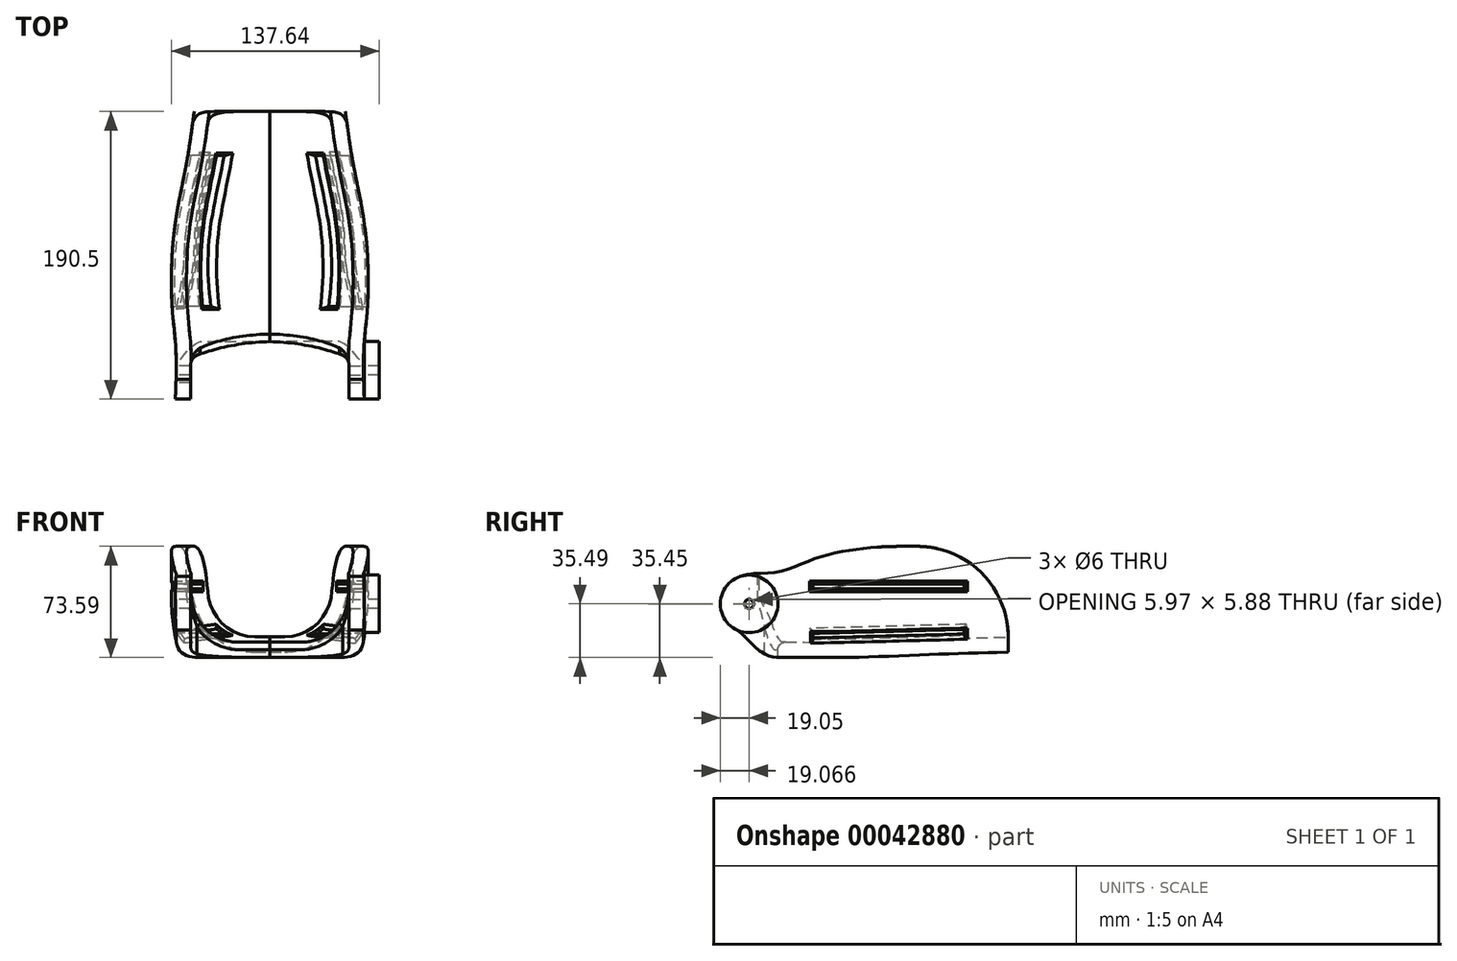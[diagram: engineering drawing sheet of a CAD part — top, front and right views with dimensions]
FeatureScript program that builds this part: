
annotation { "Feature Type Name" : "Feature", "Feature Type Description" : "" }
export const myFeature = defineFeature(function(context is Context, id is Id, definition is map)
    precondition{}
    {
        {
            assignVariable(context, id + "F0", {"name" : "FST", "anyValue" : 10 * mm});
        }
        {
            assignVariable(context, id + "F1", {"name" : "FSG", "anyValue" : 5 * mm});
        }
        {
            var Q0;
            Q0=qCreatedBy(makeId("Right.planeOp"),FACE);
            cPlane(context, id + "F2", {"entities" : qUnion([Q0]), "cplaneType" : CPlaneType.OFFSET, "offset" : (115 * mm / 2) + getVariable(context, 'FSG'), "width" : 150 * mm, "height" : 150 * mm});
        }
        {
            var Q0;
            Q0=qCreatedBy(makeId("Front.planeOp"),FACE);
            cPlane(context, id + "F3", {"entities" : qUnion([Q0]), "cplaneType" : CPlaneType.OFFSET, "offset" : 114.3 * mm, "width" : 150 * mm, "height" : 150 * mm});
        }
        {
            var Q0;
            Q0=qCreatedBy(makeId("Front.planeOp"),FACE);
            cPlane(context, id + "F4", {"entities" : qUnion([Q0]), "cplaneType" : CPlaneType.OFFSET, "offset" : 76.2 * mm, "width" : 150 * mm, "height" : 150 * mm});
        }
        {
            var Q0;
            Q0=qCreatedBy(makeId("Front.planeOp"),FACE);
            cPlane(context, id + "F5", {"entities" : qUnion([Q0]), "cplaneType" : CPlaneType.OFFSET, "offset" : (76.2 * mm) - 15 * mm, "width" : 150 * mm, "height" : 150 * mm});
        }
        {
            var Q0;
            Q0=qCreatedBy(makeId("Front.planeOp"),FACE);
            cPlane(context, id + "F6", {"entities" : qUnion([Q0]), "cplaneType" : CPlaneType.OFFSET, "offset" : (76.2 * mm) - 49 * mm, "width" : 150 * mm, "height" : 150 * mm});
        }
        {
            var Q0;
            Q0=qCreatedBy(makeId("Top.planeOp"),FACE);
            cPlane(context, id + "F7", {"entities" : qUnion([Q0]), "cplaneType" : CPlaneType.OFFSET, "offset" : 63.5 * mm + 10 * mm, "oppositeDirection" : true, "width" : 150 * mm, "height" : 150 * mm});
        }
        {
            var Q0;
            Q0=qCreatedBy(makeId("Front.planeOp"),FACE);
            cPlane(context, id + "F8", {"entities" : qUnion([Q0]), "cplaneType" : CPlaneType.OFFSET, "offset" : 76.2 * mm, "oppositeDirection" : true, "width" : 150 * mm, "height" : 150 * mm});
        }
        {
            var Q0;
            Q0=qCreatedBy(makeId("Front.planeOp"),FACE);
            cPlane(context, id + "F9", {"entities" : qUnion([Q0]), "cplaneType" : CPlaneType.OFFSET, "offset" : 76.2 * mm - 33.4 * mm, "oppositeDirection" : true, "width" : 150 * mm, "height" : 150 * mm});
        }
        {
            var Q0;
            Q0=qCreatedBy(makeId("Front.planeOp"),FACE);
            cPlane(context, id + "F10", {"entities" : qUnion([Q0]), "cplaneType" : CPlaneType.OFFSET, "offset" : 76.2 * mm - 73.4 * mm, "oppositeDirection" : true, "width" : 150 * mm, "height" : 150 * mm});
        }
        {
            var Q0;
            Q0=qCreatedBy(makeId("Top.planeOp"),FACE);
            var sketch = newSketch(context, id + "F11", { "sketchPlane" : qUnion([Q0])});
            skLineSegment(sketch, "E0", {"start": v(0, 76.2) * mm, "end": v(0, -76.2) * mm, "construction": true});
            skPoint(sketch, "E1", {"position": v(0, 0) * mm});
            skLineSegment(sketch, "E2", {"start": v(0, -76.2) * mm, "end": v(52.5, -76.2) * mm, "construction": true});
            skLineSegment(sketch, "E3", {"start": v(0, -61.2) * mm, "end": v(54, -61.2) * mm, "construction": true});
            skLineSegment(sketch, "E4", {"start": v(0, -27.2) * mm, "end": v(55, -27.2) * mm, "construction": true});
            skLineSegment(sketch, "E5", {"start": v(0, 2.8) * mm, "end": v(52.5, 2.8) * mm, "construction": true});
            skLineSegment(sketch, "E6", {"start": v(0, 42.8) * mm, "end": v(45, 42.8) * mm, "construction": true});
            skLineSegment(sketch, "E7", {"start": v(0, 76.2) * mm, "end": v(40, 76.2) * mm, "construction": true});
            skLineSegment(sketch, "E8.bottom", {"start": v(-157.02, 34.24) * mm, "end": v(-106.22, 34.24) * mm});
            skLineSegment(sketch, "E8.top", {"start": v(-157.02, -16.56) * mm, "end": v(-106.22, -16.56) * mm});
            skLineSegment(sketch, "E8.left", {"start": v(-157.02, 34.24) * mm, "end": v(-157.02, -16.56) * mm});
            skLineSegment(sketch, "E8.right", {"start": v(-106.22, 34.24) * mm, "end": v(-106.22, -16.56) * mm});
            skLineSegment(sketch, "E9", {"start": v(55, 76.2) * mm, "end": v(55, -76.2) * mm, "construction": true});
            skPoint(sketch, "E10", {"position": v(20, 76.2) * mm});
            skLineSegment(sketch, "E11", {"start": v(-60, 76.2) * mm, "end": v(-60, -76.2) * mm, "construction": true});
            skLineSegment(sketch, "E12", {"start": v(0, -95.25) * mm, "end": v(57.5, -95.25) * mm, "construction": true});
            skLineSegment(sketch, "E13", {"start": v(0, -114.3) * mm, "end": v(57.5, -114.3) * mm, "construction": true});
            skLineSegment(sketch, "E14", {"start": v(0, -84.2) * mm, "end": v(57.5, -84.2) * mm, "construction": true});
            skPoint(sketch, "E15.visualSharp", {"position": v(57.5, -84.2) * mm});
            skLineSegment(sketch, "E15.filletArc", {"start": v(57.5, -84.2) * mm, "end": v(57.5, -84.2) * mm});
            skLineSegment(sketch, "E16", {"start": v(40, 76.2) * mm, "end": v(50, 76.2) * mm});
            skLineSegment(sketch, "E17", {"start": v(45, 42.8) * mm, "end": v(55, 42.8) * mm, "construction": true});
            skLineSegment(sketch, "E18", {"start": v(52.5, 2.8) * mm, "end": v(62.5, 2.8) * mm, "construction": true});
            skLineSegment(sketch, "E19", {"start": v(55, -27.2) * mm, "end": v(65, -27.2) * mm, "construction": true});
            skLineSegment(sketch, "E20", {"start": v(54, -61.2) * mm, "end": v(64, -61.2) * mm, "construction": true});
            skLineSegment(sketch, "E21", {"start": v(52.5, -76.2) * mm, "end": v(62.5, -76.2) * mm, "construction": true});
            skLineSegment(sketch, "E22", {"start": v(57.5, -84.2) * mm, "end": v(67.5, -84.2) * mm});
            skLineSegment(sketch, "E23", {"start": v(57.5, -95.25) * mm, "end": v(67.5, -95.25) * mm});
            skLineSegment(sketch, "E24", {"start": v(57.5, -114.3) * mm, "end": v(67.5, -114.3) * mm});
            skFitSpline(sketch, "E25", {"points": [v(50, 76.2) * mm, v(55, 42.8) * mm, v(62.5, 2.8) * mm, v(65, -27.2) * mm, v(64, -61.2) * mm, v(62.5, -76.2) * mm, v(67.5, -84.2) * mm, v(67.5, -95.25) * mm, v(67.5, -114.3) * mm], "startDerivative": vector(28.82, -213.97) * mm, "endDerivative": vector(-0.1, -161.58) * mm});
            skLineSegment(sketch, "E26", {"start": v(55, -76.2) * mm, "end": v(55, -137.07) * mm, "construction": true});
            skFitSpline(sketch, "E27", {"points": [v(40, 76.2) * mm, v(45, 42.8) * mm, v(52.5, 2.8) * mm, v(55, -27.2) * mm, v(54, -61.2) * mm, v(52.5, -76.2) * mm, v(57.5, -84.2) * mm, v(57.5, -95.25) * mm, v(57.5, -114.3) * mm], "startDerivative": vector(29.26, -219.54) * mm, "endDerivative": vector(0.26, -174.77) * mm});
            skLineSegment(sketch, "E28", {"start": v(0, -114.05) * mm, "end": v(57.5, -114.05) * mm, "construction": true});
            skLineSegment(sketch, "E29", {"start": v(57.5, -114.05) * mm, "end": v(67.5, -114.05) * mm});
            skSolve(sketch);
        }
        {
            var Q0;
            Q0=qCreatedBy(id+"F3.planeOp",FACE);
            var sketch = newSketch(context, id + "F12", { "sketchPlane" : qUnion([Q0])});
            skLineSegment(sketch, "E30", {"start": v(0, 0) * mm, "end": v(52.5, 0) * mm, "construction": true});
            skLineSegment(sketch, "E31", {"start": v(52.5, 0) * mm, "end": v(62.5, 0) * mm});
            skLineSegment(sketch, "E32", {"start": v(0, 0) * mm, "end": v(0, -63.5) * mm, "construction": true});
            skLineSegment(sketch, "E33", {"start": v(0, 0) * mm, "end": v(47.5, 0) * mm, "construction": true});
            skLineSegment(sketch, "E34", {"start": v(52.5, 0) * mm, "end": v(52.5, -31.5) * mm});
            skLineSegment(sketch, "E35", {"start": v(20.5, -63.5) * mm, "end": v(0, -63.5) * mm});
            skLineSegment(sketch, "E36", {"start": v(0, -63.5) * mm, "end": v(0, -73.5) * mm});
            skArc(sketch, "E37.filletArc", {"start": v(20.5, -63.5) * mm, "mid": v(43.13, -54.13) * mm, "end": v(52.5, -31.5) * mm});
            skPoint(sketch, "E38", {"position": v(0, -35.5) * mm});
            skLineSegment(sketch, "E39", {"start": v(0, -35.5) * mm, "end": v(67.5, -35.5) * mm, "construction": true});
            skLineSegment(sketch, "E40", {"start": v(62.5, 0) * mm, "end": v(62.5, -58.5) * mm});
            skLineSegment(sketch, "E41", {"start": v(47.5, -73.5) * mm, "end": v(0, -73.5) * mm});
            skPoint(sketch, "E42.visualSharp", {"position": v(62.5, -73.5) * mm});
            skArc(sketch, "E42.filletArc", {"start": v(47.5, -73.5) * mm, "mid": v(58.1, -69.1) * mm, "end": v(62.5, -58.5) * mm});
            skSolve(sketch);
        }
        {
            var Q0;
            Q0=qCreatedBy(id+"F4.planeOp",FACE);
            var sketch = newSketch(context, id + "F13", { "sketchPlane" : qUnion([Q0])});
            skLineSegment(sketch, "E43", {"start": v(0, 0) * mm, "end": v(52.5, 0) * mm, "construction": true});
            skLineSegment(sketch, "E44", {"start": v(0, 0) * mm, "end": v(0, -63.5) * mm, "construction": true});
            skLineSegment(sketch, "E45", {"start": v(52.5, 0) * mm, "end": v(62.5, 0) * mm});
            skLineSegment(sketch, "E46", {"start": v(0, -63.5) * mm, "end": v(0, -73.5) * mm});
            skLineSegment(sketch, "E47", {"start": v(52.5, 0) * mm, "end": v(52.5, -31.5) * mm});
            skLineSegment(sketch, "E48", {"start": v(20.5, -63.5) * mm, "end": v(0, -63.5) * mm});
            skLineSegment(sketch, "E49", {"start": v(62.5, -58.5) * mm, "end": v(62.5, 0) * mm});
            skPoint(sketch, "E50.visualSharp", {"position": v(52.5, -63.5) * mm});
            skArc(sketch, "E50.filletArc", {"start": v(20.5, -63.5) * mm, "mid": v(43.13, -54.13) * mm, "end": v(52.5, -31.5) * mm});
            skLineSegment(sketch, "E51", {"start": v(47.5, -73.5) * mm, "end": v(0, -73.5) * mm});
            skPoint(sketch, "E52.visualSharp", {"position": v(62.5, -73.5) * mm});
            skArc(sketch, "E52.filletArc", {"start": v(47.5, -73.5) * mm, "mid": v(58.1, -69.1) * mm, "end": v(62.5, -58.5) * mm});
            skSolve(sketch);
        }
        {
            var Q0;
            Q0=qCreatedBy(id+"F5.planeOp",FACE);
            var sketch = newSketch(context, id + "F14", { "sketchPlane" : qUnion([Q0])});
            skLineSegment(sketch, "E53", {"start": v(0, 0) * mm, "end": v(54, 0) * mm, "construction": true});
            skLineSegment(sketch, "E54", {"start": v(0, 0) * mm, "end": v(0, -63.5) * mm, "construction": true});
            skLineSegment(sketch, "E55", {"start": v(54, 0) * mm, "end": v(64, 0) * mm});
            skLineSegment(sketch, "E56", {"start": v(0, -63.5) * mm, "end": v(0, -73.5) * mm});
            skLineSegment(sketch, "E57", {"start": v(54, 0) * mm, "end": v(54, -31.5) * mm});
            skLineSegment(sketch, "E58", {"start": v(22, -63.5) * mm, "end": v(0, -63.5) * mm});
            skLineSegment(sketch, "E59", {"start": v(64, 0) * mm, "end": v(64, -48.5) * mm});
            skLineSegment(sketch, "E60", {"start": v(39, -73.5) * mm, "end": v(0, -73.5) * mm});
            skPoint(sketch, "E61.visualSharp", {"position": v(54, -63.5) * mm});
            skArc(sketch, "E61.filletArc", {"start": v(22, -63.5) * mm, "mid": v(44.63, -54.13) * mm, "end": v(54, -31.5) * mm});
            skPoint(sketch, "E62.visualSharp", {"position": v(64, -73.5) * mm});
            skArc(sketch, "E62.filletArc", {"start": v(39, -73.5) * mm, "mid": v(56.68, -66.18) * mm, "end": v(64, -48.5) * mm});
            skSolve(sketch);
        }
        {
            var Q0;
            Q0=qCreatedBy(id+"F6.planeOp",FACE);
            var sketch = newSketch(context, id + "F15", { "sketchPlane" : qUnion([Q0])});
            skLineSegment(sketch, "E63", {"start": v(0, 0) * mm, "end": v(55, 0) * mm, "construction": true});
            skLineSegment(sketch, "E64", {"start": v(0, 0) * mm, "end": v(0, -63.5) * mm, "construction": true});
            skLineSegment(sketch, "E65", {"start": v(55, 0) * mm, "end": v(65, 0) * mm});
            skLineSegment(sketch, "E66", {"start": v(0, -63.5) * mm, "end": v(0, -73.5) * mm});
            skLineSegment(sketch, "E67", {"start": v(55, 0) * mm, "end": v(55, -31.5) * mm});
            skLineSegment(sketch, "E68", {"start": v(23, -63.5) * mm, "end": v(0, -63.5) * mm});
            skLineSegment(sketch, "E69", {"start": v(65, 0) * mm, "end": v(65, -31.5) * mm});
            skLineSegment(sketch, "E70", {"start": v(23, -73.5) * mm, "end": v(0, -73.5) * mm});
            skPoint(sketch, "E71.visualSharp", {"position": v(55, -63.5) * mm});
            skArc(sketch, "E71.filletArc", {"start": v(23, -63.5) * mm, "mid": v(45.63, -54.13) * mm, "end": v(55, -31.5) * mm});
            skPoint(sketch, "E72.visualSharp", {"position": v(65, -73.5) * mm});
            skArc(sketch, "E72.filletArc", {"start": v(23, -73.5) * mm, "mid": v(52.7, -61.2) * mm, "end": v(65, -31.5) * mm});
            skSolve(sketch);
        }
        {
            var Q0;
            Q0=qCreatedBy(id+"F8.planeOp",FACE);
            var sketch = newSketch(context, id + "F16", { "sketchPlane" : qUnion([Q0])});
            skLineSegment(sketch, "E73", {"start": v(0, 0) * mm, "end": v(0, -60) * mm, "construction": true});
            skLineSegment(sketch, "E74", {"start": v(0, 0) * mm, "end": v(40, 0) * mm, "construction": true});
            skLineSegment(sketch, "E75", {"start": v(0, -60) * mm, "end": v(10, -60) * mm});
            skLineSegment(sketch, "E76", {"start": v(40, 0) * mm, "end": v(50, 0) * mm});
            skLineSegment(sketch, "E77", {"start": v(0, -60) * mm, "end": v(0, -70) * mm});
            skLineSegment(sketch, "E78", {"start": v(0, -70) * mm, "end": v(10, -70) * mm});
            skLineSegment(sketch, "E79", {"start": v(50, -30) * mm, "end": v(50, 0) * mm});
            skLineSegment(sketch, "E80", {"start": v(40, -30) * mm, "end": v(40, 0) * mm});
            skPoint(sketch, "E81.visualSharp", {"position": v(40, -60) * mm});
            skArc(sketch, "E81.filletArc", {"start": v(10, -60) * mm, "mid": v(31.21, -51.21) * mm, "end": v(40, -30) * mm});
            skPoint(sketch, "E82.visualSharp", {"position": v(50, -70) * mm});
            skArc(sketch, "E82.filletArc", {"start": v(10, -70) * mm, "mid": v(38.28, -58.28) * mm, "end": v(50, -30) * mm});
            skSolve(sketch);
        }
        {
            var Q0;
            Q0=qCreatedBy(id+"F9.planeOp",FACE);
            var sketch = newSketch(context, id + "F17", { "sketchPlane" : qUnion([Q0])});
            skLineSegment(sketch, "E83", {"start": v(0, 0) * mm, "end": v(45, 0) * mm, "construction": true});
            skLineSegment(sketch, "E84", {"start": v(0, 0) * mm, "end": v(0, -61) * mm, "construction": true});
            skLineSegment(sketch, "E85", {"start": v(45, 0) * mm, "end": v(55, 0) * mm});
            skLineSegment(sketch, "E86", {"start": v(0, -61) * mm, "end": v(0, -71) * mm});
            skLineSegment(sketch, "E87", {"start": v(45, 0) * mm, "end": v(45, -31) * mm});
            skLineSegment(sketch, "E88", {"start": v(15, -61) * mm, "end": v(0, -61) * mm});
            skLineSegment(sketch, "E89", {"start": v(55, 0) * mm, "end": v(55, -31) * mm});
            skLineSegment(sketch, "E90", {"start": v(15, -71) * mm, "end": v(0, -71) * mm});
            skPoint(sketch, "E91.visualSharp", {"position": v(45, -61) * mm});
            skArc(sketch, "E91.filletArc", {"start": v(15, -61) * mm, "mid": v(36.21, -52.21) * mm, "end": v(45, -31) * mm});
            skPoint(sketch, "E92.visualSharp", {"position": v(55, -71) * mm});
            skArc(sketch, "E92.filletArc", {"start": v(15, -71) * mm, "mid": v(43.28, -59.28) * mm, "end": v(55, -31) * mm});
            skSolve(sketch);
        }
        {
            var Q0;
            Q0=qCreatedBy(id+"F10.planeOp",FACE);
            var sketch = newSketch(context, id + "F18", { "sketchPlane" : qUnion([Q0])});
            skLineSegment(sketch, "E93", {"start": v(0, 0) * mm, "end": v(52.5, 0) * mm, "construction": true});
            skLineSegment(sketch, "E94", {"start": v(0, 0) * mm, "end": v(0, -62.5) * mm, "construction": true});
            skLineSegment(sketch, "E95", {"start": v(52.5, 0) * mm, "end": v(62.5, 0) * mm});
            skLineSegment(sketch, "E96", {"start": v(0, -62.5) * mm, "end": v(0, -72.5) * mm});
            skLineSegment(sketch, "E97", {"start": v(52.5, 0) * mm, "end": v(52.5, -31.5) * mm});
            skLineSegment(sketch, "E98", {"start": v(21.5, -62.5) * mm, "end": v(0, -62.5) * mm});
            skLineSegment(sketch, "E99", {"start": v(62.5, 0) * mm, "end": v(62.5, -31.5) * mm});
            skLineSegment(sketch, "E100", {"start": v(21.5, -72.5) * mm, "end": v(0, -72.5) * mm});
            skPoint(sketch, "E101.visualSharp", {"position": v(52.5, -62.5) * mm});
            skArc(sketch, "E101.filletArc", {"start": v(21.5, -62.5) * mm, "mid": v(43.42, -53.42) * mm, "end": v(52.5, -31.5) * mm});
            skPoint(sketch, "E102.visualSharp", {"position": v(62.5, -72.5) * mm});
            skArc(sketch, "E102.filletArc", {"start": v(21.5, -72.5) * mm, "mid": v(50.5, -60.5) * mm, "end": v(62.5, -31.5) * mm});
            skSolve(sketch);
        }
        {
            var Q0;
            Q0=qCreatedBy(makeId("Right.planeOp"),FACE);
            var sketch = newSketch(context, id + "F19", { "sketchPlane" : qUnion([Q0])});
            skLineSegment(sketch, "E103", {"start": v(-76.2, 0) * mm, "end": v(76.2, 0) * mm, "construction": true});
            skLineSegment(sketch, "E104", {"start": v(76.2, 0) * mm, "end": v(76.2, -60) * mm, "construction": true});
            skLineSegment(sketch, "E105", {"start": v(42.8, 0) * mm, "end": v(42.8, -61) * mm, "construction": true});
            skLineSegment(sketch, "E106", {"start": v(2.8, 0) * mm, "end": v(2.8, -62.5) * mm, "construction": true});
            skLineSegment(sketch, "E107", {"start": v(-27.2, 0) * mm, "end": v(-27.2, -63.5) * mm, "construction": true});
            skLineSegment(sketch, "E108", {"start": v(-61.2, 0) * mm, "end": v(-61.2, -63.5) * mm, "construction": true});
            skLineSegment(sketch, "E109", {"start": v(-76.2, 0) * mm, "end": v(-76.2, -63.5) * mm, "construction": true});
            skPoint(sketch, "E110", {"position": v(0, 0) * mm});
            skLineSegment(sketch, "E111", {"start": v(76.2, -60) * mm, "end": v(76.2, -70) * mm});
            skLineSegment(sketch, "E112", {"start": v(42.8, -61) * mm, "end": v(42.8, -71) * mm});
            skLineSegment(sketch, "E113", {"start": v(2.8, -62.5) * mm, "end": v(2.8, -72.5) * mm});
            skLineSegment(sketch, "E114", {"start": v(-27.2, -63.5) * mm, "end": v(-27.2, -73.5) * mm});
            skLineSegment(sketch, "E115", {"start": v(-61.2, -63.5) * mm, "end": v(-61.2, -73.5) * mm});
            skLineSegment(sketch, "E116", {"start": v(-76.2, -63.5) * mm, "end": v(-76.2, -73.5) * mm});
            skLineSegment(sketch, "E117", {"start": v(-84.2, 0) * mm, "end": v(-84.2, -63.5) * mm, "construction": true});
            skLineSegment(sketch, "E118", {"start": v(-84.2, -63.5) * mm, "end": v(-84.2, -73.5) * mm});
            skLineSegment(sketch, "E119", {"start": v(-95.25, 0) * mm, "end": v(-95.25, -63.5) * mm, "construction": true});
            skLineSegment(sketch, "E120", {"start": v(-114.3, 0) * mm, "end": v(-114.3, -63.5) * mm, "construction": true});
            skLineSegment(sketch, "E121", {"start": v(-95.25, -63.5) * mm, "end": v(-95.25, -73.5) * mm});
            skLineSegment(sketch, "E122", {"start": v(-114.3, -63.5) * mm, "end": v(-114.3, -73.5) * mm});
            skFitSpline(sketch, "E123", {"points": [v(76.2, -60) * mm, v(42.8, -61) * mm, v(2.8, -62.5) * mm, v(-27.2, -63.5) * mm, v(-61.2, -63.5) * mm, v(-76.2, -63.5) * mm, v(-84.2, -63.5) * mm, v(-95.25, -63.5) * mm, v(-114.3, -63.5) * mm], "startDerivative": vector(-217.44, -6.1) * mm, "endDerivative": vector(-173.87, 0) * mm});
            skFitSpline(sketch, "E124", {"points": [v(76.2, -70) * mm, v(42.8, -71) * mm, v(2.8, -72.5) * mm, v(-27.2, -73.5) * mm, v(-61.2, -73.5) * mm, v(-76.2, -73.5) * mm, v(-84.2, -73.5) * mm, v(-95.25, -73.5) * mm, v(-114.3, -73.5) * mm], "startDerivative": vector(-217.36, -6.1) * mm, "endDerivative": vector(-173.09, 0) * mm});
            skLineSegment(sketch, "E125.bottom", {"start": v(-173.81, 0) * mm, "end": v(-223.81, 0) * mm, "construction": true});
            skLineSegment(sketch, "E125.top", {"start": v(-173.81, -50) * mm, "end": v(-223.81, -50) * mm, "construction": true});
            skLineSegment(sketch, "E125.left", {"start": v(-173.81, 0) * mm, "end": v(-173.81, -50) * mm, "construction": true});
            skLineSegment(sketch, "E125.right", {"start": v(-223.81, 0) * mm, "end": v(-223.81, -50) * mm, "construction": true});
            skSolve(sketch);
        }
        {
            var Q0;
            Q0=makeQuery(id+"F16.imprint","IMPRINT",FACE,{"disambiguationData":[TD([[makeQuery(id+"F16.imprint","IMPRINT",EDGE,{"derivedFrom":sQuery(id+"F16.wireOp",EDGE,"E75")}),-1.0]])]});
            var Q1;
            Q1=makeQuery(id+"F17.imprint","IMPRINT",FACE,{"disambiguationData":[TD([[makeQuery(id+"F17.imprint","IMPRINT",EDGE,{"derivedFrom":sQuery(id+"F17.wireOp",EDGE,"E85")}),-1.0]])]});
            var Q2;
            Q2=makeQuery(id+"F18.imprint","IMPRINT",FACE,{"disambiguationData":[TD([[makeQuery(id+"F18.imprint","IMPRINT",EDGE,{"derivedFrom":sQuery(id+"F18.wireOp",EDGE,"E95")}),-1.0]])]});
            var Q3;
            Q3=makeQuery(id+"F15.imprint","IMPRINT",FACE,{"disambiguationData":[TD([[makeQuery(id+"F15.imprint","IMPRINT",EDGE,{"derivedFrom":sQuery(id+"F15.wireOp",EDGE,"E65")}),-1.0]])]});
            var Q4;
            Q4=makeQuery(id+"F14.imprint","IMPRINT",FACE,{"disambiguationData":[TD([[makeQuery(id+"F14.imprint","IMPRINT",EDGE,{"derivedFrom":sQuery(id+"F14.wireOp",EDGE,"E55")}),-1.0]])]});
            var Q5;
            Q5=makeQuery(id+"F13.imprint","IMPRINT",FACE,{"disambiguationData":[TD([[makeQuery(id+"F13.imprint","IMPRINT",EDGE,{"derivedFrom":sQuery(id+"F13.wireOp",EDGE,"E45")}),-1.0]])]});
            var Q6;
            Q6=makeQuery(id+"F12.imprint","IMPRINT",FACE,{"disambiguationData":[TD([[makeQuery(id+"F12.imprint","IMPRINT",EDGE,{"derivedFrom":sQuery(id+"F12.wireOp",EDGE,"E31")}),-1.0]])]});
            loft(context, id + "F20", {"sheetProfilesArray" : [{ "sheetProfileEntities" : qUnion([Q0]) }, { "sheetProfileEntities" : qUnion([Q1]) }, { "sheetProfileEntities" : qUnion([Q2]) }, { "sheetProfileEntities" : qUnion([Q3]) }, { "sheetProfileEntities" : qUnion([Q4]) }, { "sheetProfileEntities" : qUnion([Q5]) }, { "sheetProfileEntities" : qUnion([Q6]) }]});
        }
        {
            var Q0;
            Q0=makeQuery(id+"F20.opLoft","MID_CAP_EDGE",EDGE,{"disambiguationData":[OSD([sQuery(id+"F16.wireOp",EDGE,"E76"),sQuery(id+"F16.wireOp",EDGE,"E79"),sQuery(id+"F16.wireOp",EDGE,"E80")])],"capPos":0.0});
            fillet(context, id + "F21", {"entities" : qUnion([Q0]), "radius" : 60 * mm, "tangentPropagation" : true, "allowEdgeOverflow" : false});
        }
        {
            var Q0;
            Q0=qCreatedBy(id+"F2.planeOp",FACE);
            var sketch = newSketch(context, id + "F22", { "sketchPlane" : qUnion([Q0])});
            skCircle(sketch, "E126", {"center": v(-95.25, -38.1) * mm, "radius": 19.05 * mm});
            skLineSegment(sketch, "E127", {"start": v(-76.2, 0) * mm, "end": v(76.2, 0) * mm, "construction": true});
            skLineSegment(sketch, "E128", {"start": v(-76.2, 0) * mm, "end": v(-76.2, -63.5) * mm, "construction": true});
            skLineSegment(sketch, "E129", {"start": v(-76.2, -63.5) * mm, "end": v(-76.2, -73.5) * mm, "construction": true});
            skLineSegment(sketch, "E130", {"start": v(-76.2, -73.5) * mm, "end": v(-114.3, -73.5) * mm, "construction": true});
            skLineSegment(sketch, "E131", {"start": v(-76.2, -19.05) * mm, "end": v(-114.3, -19.05) * mm, "construction": true});
            skLineSegment(sketch, "E132", {"start": v(-76.2, 0) * mm, "end": v(-114.3, 0) * mm, "construction": true});
            skLineSegment(sketch, "E133", {"start": v(-95.25, -38.1) * mm, "end": v(-114.3, -38.1) * mm, "construction": true});
            skLineSegment(sketch, "E134", {"start": v(-95.25, -38.1) * mm, "end": v(-95.25, -73.5) * mm, "construction": true});
            skLineSegment(sketch, "E135", {"start": v(-127.04, -54.43) * mm, "end": v(-127.04, -88.5) * mm});
            skLineSegment(sketch, "E136", {"start": v(-127.04, -54.43) * mm, "end": v(-127.04, 0) * mm});
            skLineSegment(sketch, "E137", {"start": v(-127.04, 0) * mm, "end": v(0, 0) * mm, "construction": true});
            skLineSegment(sketch, "E138", {"start": v(-51.2, 0) * mm, "end": v(-51.2, -8) * mm, "construction": true});
            skPoint(sketch, "E139", {"position": v(-76.2, -17) * mm});
            skLineSegment(sketch, "E140", {"start": v(-16.2, 0) * mm, "end": v(-16.2, -1) * mm, "construction": true});
            skLineSegment(sketch, "E141", {"start": v(3.8, 0) * mm, "end": v(3.8, 0) * mm});
            skPoint(sketch, "E142", {"position": v(13.8, 0) * mm});
            skLineSegment(sketch, "E143", {"start": v(-127.04, 0) * mm, "end": v(-127.04, 22.7) * mm});
            skLineSegment(sketch, "E144", {"start": v(-127.04, 22.7) * mm, "end": v(13.8, 22.7) * mm});
            skLineSegment(sketch, "E145", {"start": v(13.8, 22.7) * mm, "end": v(13.8, 0) * mm});
            skCircle(sketch, "E146", {"center": v(-95.25, -38.1) * mm, "radius": 3 * mm});
            skLineSegment(sketch, "E147", {"start": v(-95.25, -38.1) * mm, "end": v(-101.14, -19.98) * mm, "construction": true});
            skLineSegment(sketch, "E148", {"start": v(-95.25, -38.1) * mm, "end": v(-95.25, -19.05) * mm, "construction": true});
            skFitSpline(sketch, "E149", {"points": [v(-101.14, -19.98) * mm, v(-76.2, -17) * mm, v(-51.2, -8) * mm, v(-16.2, -1) * mm, v(3.8, 0) * mm, v(13.8, 0) * mm], "startDerivative": vector(117.64, 43.18) * mm, "endDerivative": vector(70.79, -0.21) * mm});
            skLineSegment(sketch, "E150", {"start": v(-95.25, -38.1) * mm, "end": v(-103.3, -55.37) * mm, "construction": true});
            skLineSegment(sketch, "E151", {"start": v(-127.04, -88.5) * mm, "end": v(-76.2, -88.5) * mm});
            skLineSegment(sketch, "E152", {"start": v(-76.2, -73.5) * mm, "end": v(-76.2, -88.5) * mm});
            skFitSpline(sketch, "E153", {"points": [v(-103.3, -55.37) * mm, v(-76.2, -73.5) * mm], "startDerivative": vector(27.1, -18.13) * mm, "endDerivative": vector(39, 0) * mm});
            skSolve(sketch);
        }
        {
            var Q0;
            Q0=makeQuery(id+"F22.imprint","IMPRINT",FACE,{"disambiguationData":[TD([[makeQuery(id+"F22.imprint","IMPRINT",EDGE,{"derivedFrom":sQuery(id+"F22.wireOp",EDGE,"E135")}),1.0]])]});
            extrude(context, id + "F23", {"entities" : qUnion([Q0]), "operationType" : NewBodyOperationType.REMOVE, "endBound" : BoundingType.SYMMETRIC, "oppositeDirection" : true, "depth" : 140 * mm});
        }
        {
            var Q0;
            Q0=makeQuery(id+"F22.imprint","IMPRINT",FACE,{"disambiguationData":[TD([[makeQuery(id+"F22.imprint","IMPRINT",EDGE,{"derivedFrom":sQuery(id+"F22.wireOp",EDGE,"E146")}),1.0]])]});
            extrude(context, id + "F24", {"entities" : qUnion([Q0]), "operationType" : NewBodyOperationType.REMOVE, "endBound" : BoundingType.THROUGH_ALL, "oppositeDirection" : true, "depth" : 25 * mm});
        }
        {
            var Q0;
            Q0=qCreatedBy(id+"F7.planeOp",FACE);
            var sketch = newSketch(context, id + "F25", { "sketchPlane" : qUnion([Q0])});
            skLineSegment(sketch, "E154", {"start": v(0, 76.2) * mm, "end": v(0, -76.2) * mm});
            skLineSegment(sketch, "E155", {"start": v(0, -114.3) * mm, "end": v(52.5, -114.3) * mm});
            skLineSegment(sketch, "E156", {"start": v(0, -76.2) * mm, "end": v(0, -114.3) * mm, "construction": true});
            skLineSegment(sketch, "E157", {"start": v(0, -95.25) * mm, "end": v(52.5, -95.25) * mm, "construction": true});
            skLineSegment(sketch, "E158.rect.bottom", {"start": v(62.5, -98.25) * mm, "end": v(52.5, -98.25) * mm, "construction": true});
            skLineSegment(sketch, "E158.rect.top", {"start": v(62.5, -92.25) * mm, "end": v(52.5, -92.25) * mm, "construction": true});
            skLineSegment(sketch, "E158.rect.left", {"start": v(62.5, -98.25) * mm, "end": v(62.5, -92.25) * mm, "construction": true});
            skLineSegment(sketch, "E158.rect.right", {"start": v(52.5, -98.25) * mm, "end": v(52.5, -92.25) * mm, "construction": true});
            skPoint(sketch, "E158.rect.middle", {"position": v(57.5, -95.25) * mm});
            skLineSegment(sketch, "E159", {"start": v(52.5, -95.25) * mm, "end": v(52.5, -92.25) * mm, "construction": true});
            skLineSegment(sketch, "E160", {"start": v(0, -72.2) * mm, "end": v(-24.84, -72.2) * mm, "construction": true});
            skLineSegment(sketch, "E161", {"start": v(0, -72.2) * mm, "end": v(0, -114.3) * mm});
            skLineSegment(sketch, "E162", {"start": v(52.5, -114.3) * mm, "end": v(52.5, -92.25) * mm});
            skArc(sketch, "E163", {"start": v(52.5, -92.25) * mm, "mid": v(51.33, -88.09) * mm, "end": v(48.17, -85.14) * mm});
            skArc(sketch, "E164", {"start": v(48.17, -85.14) * mm, "mid": v(24.45, -78.7) * mm, "end": v(0, -76.2) * mm});
            skSolve(sketch);
        }
        {
            var Q0;
            {var subQ7=sQuery(id+"F25.wireOp",EDGE,"E155");Q0=makeQuery(id+"F25.imprint","IMPRINT",FACE,{"disambiguationData":[TD([[makeQuery(id+"F25.imprint","IMPRINT",EDGE,{"derivedFrom":subQ7}),1.0]])]});}
            var Q1;
            {var subQ0=sQuery(id+"F25.wireOp",EDGE,"6ab98432-ff88-4967-8b7e-415d656d9d2a");var subQ1=makeQuery(id+"F25.imprint","INTERSECT",VERTEX,{"derivedFrom":[subQ0,sQuery(id+"F25.wireOp",EDGE,"E162")]});Q1=makeQuery(id+"F25.imprint","IMPRINT",FACE,{"disambiguationData":[TD([[makeQuery(id+"F25.imprint","IMPRINT",EDGE,{"disambiguationData":[TD([[subQ1,-1.0]])],"derivedFrom":subQ0}),1.0]])]});}
            var Q2;
            {var subQ3=sQuery(id+"F25.wireOp",EDGE,"E161");var subQ6=makeQuery(id+"F25.imprint","IMPRINT",VERTEX,{"derivedFrom":subQ3});Q2=makeQuery(id+"F25.imprint","IMPRINT",FACE,{"disambiguationData":[TD([[makeQuery(id+"F25.imprint","IMPRINT",EDGE,{"disambiguationData":[TD([[subQ6,1.0]])],"derivedFrom":subQ3}),1.0]])]});}
            var Q3;
            {var subQ0=sQuery(id+"F25.wireOp",EDGE,"E161");var subQ1=sQuery(id+"F25.wireOp",EDGE,"4ed179fe-1dec-4f78-bcb3-8e963e810ee6");var subQ2=makeQuery(id+"F25.imprint","INTERSECT",VERTEX,{"disambiguationData":[OD(0.0)],"derivedFrom":[subQ1,subQ0]});Q3=makeQuery(id+"F25.imprint","IMPRINT",FACE,{"disambiguationData":[TD([[makeQuery(id+"F25.imprint","IMPRINT",EDGE,{"disambiguationData":[TD([[subQ2,1.0]])],"derivedFrom":subQ1}),1.0]])]});}
            extrude(context, id + "F26", {"entities" : qUnion([Q0, Q1, Q2, Q3]), "operationType" : NewBodyOperationType.REMOVE, "endBound" : BoundingType.SYMMETRIC, "oppositeDirection" : true, "depth" : 127 * mm});
        }
        {
            var Q0;
            Q0=makeQuery(id+"F26.boolean.opBoolean","INTERSECT",EDGE,{"derivedFrom":[makeQuery(id+"F20.opLoft","SWEPT_FACE",FACE,{"disambiguationData":[OSD([sQuery(id+"F16.wireOp",EDGE,"E76"),sQuery(id+"F16.wireOp",EDGE,"E80"),sQuery(id+"F16.wireOp",EDGE,"E81.filletArc"),sQuery(id+"F17.wireOp",EDGE,"E85"),sQuery(id+"F17.wireOp",EDGE,"E87"),sQuery(id+"F17.wireOp",EDGE,"E91.filletArc")])]}),makeQuery(id+"F26.opExtrude","SWEPT_FACE",FACE,{"disambiguationData":[OSD([sQuery(id+"F25.wireOp",EDGE,"E164")])]})]});
            var Q1;
            Q1=makeQuery(id+"F26.boolean.opBoolean","INTERSECT",EDGE,{"derivedFrom":[makeQuery(id+"F20.opLoft","SWEPT_FACE",FACE,{"disambiguationData":[OSD([sQuery(id+"F16.wireOp",EDGE,"E76"),sQuery(id+"F16.wireOp",EDGE,"E80"),sQuery(id+"F16.wireOp",EDGE,"E81.filletArc"),sQuery(id+"F17.wireOp",EDGE,"E85"),sQuery(id+"F17.wireOp",EDGE,"E87"),sQuery(id+"F17.wireOp",EDGE,"E91.filletArc")])]}),makeQuery(id+"F26.opExtrude","SWEPT_FACE",FACE,{"disambiguationData":[OSD([sQuery(id+"F25.wireOp",EDGE,"E163")])]})]});
            fillet(context, id + "F27", {"entities" : qUnion([Q0, Q1]), "radius" : 5 * mm, "tangentPropagation" : true, "allowEdgeOverflow" : false});
        }
        {
            var Q0;
            Q0=qCreatedBy(id+"F2.planeOp",FACE);
            var sketch = newSketch(context, id + "F28", { "sketchPlane" : qUnion([Q0])});
            skLineSegment(sketch, "E165", {"start": v(-76.2, 0) * mm, "end": v(76.2, 0) * mm, "construction": true});
            skLineSegment(sketch, "E166", {"start": v(-76.2, 0) * mm, "end": v(-76.2, -63.5) * mm, "construction": true});
            skCircle(sketch, "E167.0", {"center": v(-95.25, -38.1) * mm, "radius": 19.05 * mm});
            skCircle(sketch, "E168.0", {"center": v(-95.25, -38.1) * mm, "radius": 3 * mm});
            skSolve(sketch);
        }
        {
            var Q0;
            Q0=makeQuery(id+"F28.imprint","IMPRINT",FACE,{"disambiguationData":[TD([[makeQuery(id+"F28.imprint","IMPRINT",EDGE,{"derivedFrom":sQuery(id+"F28.wireOp",EDGE,"E167.0")}),1.0]])]});
            extrude(context, id + "F29", {"entities" : qUnion([Q0]), "depth" : getVariable(context, 'FST')});
        }
        {
            var Q0;
            Q0=qCreatedBy(makeId("Right.planeOp"),FACE);
            var sketch = newSketch(context, id + "F30", { "sketchPlane" : qUnion([Q0])});
            skLineSegment(sketch, "E169.bottom", {"start": v(47, -25) * mm, "end": v(-53, -25) * mm});
            skLineSegment(sketch, "E169.top", {"start": v(47, -28) * mm, "end": v(-53, -28) * mm});
            skLineSegment(sketch, "E169.left", {"start": v(47, -25) * mm, "end": v(47, -28) * mm});
            skLineSegment(sketch, "E169.right", {"start": v(-53, -25) * mm, "end": v(-53, -28) * mm});
            skFitSpline(sketch, "E170.0", {"points": [v(-27.2, -63.5) * mm, v(-29.84, -63.54) * mm, v(-32.67, -63.57) * mm, v(-35.7, -63.58) * mm, v(-38.2, -63.6) * mm, v(-41.04, -63.6) * mm, v(-44.2, -63.58) * mm, v(-45.08, -63.58) * mm, v(-46.02, -63.58) * mm, v(-47.04, -63.57) * mm, v(-48.2, -63.56) * mm, v(-50.08, -63.55) * mm, v(-52.7, -63.54) * mm, v(-56.4, -63.52) * mm, v(-59.23, -63.5) * mm, v(-61.2, -63.5) * mm], "construction": true});
            skLineSegment(sketch, "E171", {"start": v(-27.2, -63.5) * mm, "end": v(-61.2, -63.5) * mm, "construction": true});
            skLineSegment(sketch, "E172", {"start": v(-53, 0) * mm, "end": v(47, 0) * mm, "construction": true});
            skLineSegment(sketch, "E173.left", {"start": v(47, -55) * mm, "end": v(47, -58) * mm});
            skLineSegment(sketch, "E174", {"start": v(47, -58) * mm, "end": v(-53, -60.62) * mm});
            skLineSegment(sketch, "E175", {"start": v(-53, -60.62) * mm, "end": v(-53, -57.62) * mm});
            skLineSegment(sketch, "E176", {"start": v(-53, -57.62) * mm, "end": v(47, -55) * mm});
            skSolve(sketch);
        }
        {
            var Q0;
            Q0=makeQuery(id+"F30.imprint","IMPRINT",FACE,{"disambiguationData":[TD([[makeQuery(id+"F30.imprint","IMPRINT",EDGE,{"derivedFrom":sQuery(id+"F30.wireOp",EDGE,"E169.bottom")}),1.0]])]});
            var Q1;
            Q1=makeQuery(id+"F30.imprint","IMPRINT",FACE,{"disambiguationData":[TD([[makeQuery(id+"F30.imprint","IMPRINT",EDGE,{"derivedFrom":sQuery(id+"F30.wireOp",EDGE,"E173.left")}),-1.0]])]});
            extrude(context, id + "F31", {"entities" : qUnion([Q0, Q1]), "operationType" : NewBodyOperationType.REMOVE, "endBound" : BoundingType.SYMMETRIC, "oppositeDirection" : true, "depth" : 140 * mm});
        }
        {
            var Q0;
            Q0=makeQuery(id+"F31.boolean.opBoolean","INTERSECT",EDGE,{"derivedFrom":[makeQuery(id+"F20.opLoft","SWEPT_FACE",FACE,{"disambiguationData":[OSD([sQuery(id+"F16.wireOp",EDGE,"E77"),sQuery(id+"F16.wireOp",EDGE,"E78"),sQuery(id+"F16.wireOp",EDGE,"E82.filletArc"),sQuery(id+"F17.wireOp",EDGE,"E86"),sQuery(id+"F17.wireOp",EDGE,"E90"),sQuery(id+"F17.wireOp",EDGE,"E92.filletArc")])]}),makeQuery(id+"F31.opExtrude","SWEPT_FACE",FACE,{"disambiguationData":[OSD([sQuery(id+"F30.wireOp",EDGE,"E169.bottom")])]})]});
            var Q1;
            Q1=makeQuery(id+"F31.boolean.opBoolean","INTERSECT",EDGE,{"derivedFrom":[makeQuery(id+"F20.opLoft","SWEPT_FACE",FACE,{"disambiguationData":[OSD([sQuery(id+"F16.wireOp",EDGE,"E77"),sQuery(id+"F16.wireOp",EDGE,"E78"),sQuery(id+"F16.wireOp",EDGE,"E82.filletArc"),sQuery(id+"F17.wireOp",EDGE,"E86"),sQuery(id+"F17.wireOp",EDGE,"E90"),sQuery(id+"F17.wireOp",EDGE,"E92.filletArc")])]}),makeQuery(id+"F31.opExtrude","SWEPT_FACE",FACE,{"disambiguationData":[OSD([sQuery(id+"F30.wireOp",EDGE,"E169.left")])]})]});
            var Q2;
            Q2=makeQuery(id+"F31.boolean.opBoolean","INTERSECT",EDGE,{"derivedFrom":[makeQuery(id+"F20.opLoft","SWEPT_FACE",FACE,{"disambiguationData":[OSD([sQuery(id+"F16.wireOp",EDGE,"E77"),sQuery(id+"F16.wireOp",EDGE,"E78"),sQuery(id+"F16.wireOp",EDGE,"E82.filletArc"),sQuery(id+"F17.wireOp",EDGE,"E86"),sQuery(id+"F17.wireOp",EDGE,"E90"),sQuery(id+"F17.wireOp",EDGE,"E92.filletArc")])]}),makeQuery(id+"F31.opExtrude","SWEPT_FACE",FACE,{"disambiguationData":[OSD([sQuery(id+"F30.wireOp",EDGE,"E169.top")])]})]});
            var Q3;
            Q3=makeQuery(id+"F31.boolean.opBoolean","INTERSECT",EDGE,{"derivedFrom":[makeQuery(id+"F20.opLoft","SWEPT_FACE",FACE,{"disambiguationData":[OSD([sQuery(id+"F16.wireOp",EDGE,"E77"),sQuery(id+"F16.wireOp",EDGE,"E78"),sQuery(id+"F16.wireOp",EDGE,"E82.filletArc"),sQuery(id+"F17.wireOp",EDGE,"E86"),sQuery(id+"F17.wireOp",EDGE,"E90"),sQuery(id+"F17.wireOp",EDGE,"E92.filletArc")])]}),makeQuery(id+"F31.opExtrude","SWEPT_FACE",FACE,{"disambiguationData":[OSD([sQuery(id+"F30.wireOp",EDGE,"E169.right")])]})]});
            var Q4;
            Q4=makeQuery(id+"F31.boolean.opBoolean","INTERSECT",EDGE,{"derivedFrom":[makeQuery(id+"F20.opLoft","SWEPT_FACE",FACE,{"disambiguationData":[OSD([sQuery(id+"F16.wireOp",EDGE,"E76"),sQuery(id+"F16.wireOp",EDGE,"E80"),sQuery(id+"F16.wireOp",EDGE,"E81.filletArc"),sQuery(id+"F17.wireOp",EDGE,"E85"),sQuery(id+"F17.wireOp",EDGE,"E87"),sQuery(id+"F17.wireOp",EDGE,"E91.filletArc")])]}),makeQuery(id+"F31.opExtrude","SWEPT_FACE",FACE,{"disambiguationData":[OSD([sQuery(id+"F30.wireOp",EDGE,"E169.top")])]})]});
            var Q5;
            Q5=makeQuery(id+"F31.boolean.opBoolean","INTERSECT",EDGE,{"derivedFrom":[makeQuery(id+"F20.opLoft","SWEPT_FACE",FACE,{"disambiguationData":[OSD([sQuery(id+"F16.wireOp",EDGE,"E76"),sQuery(id+"F16.wireOp",EDGE,"E80"),sQuery(id+"F16.wireOp",EDGE,"E81.filletArc"),sQuery(id+"F17.wireOp",EDGE,"E85"),sQuery(id+"F17.wireOp",EDGE,"E87"),sQuery(id+"F17.wireOp",EDGE,"E91.filletArc")])]}),makeQuery(id+"F31.opExtrude","SWEPT_FACE",FACE,{"disambiguationData":[OSD([sQuery(id+"F30.wireOp",EDGE,"E169.left")])]})]});
            var Q6;
            Q6=makeQuery(id+"F31.boolean.opBoolean","INTERSECT",EDGE,{"derivedFrom":[makeQuery(id+"F20.opLoft","SWEPT_FACE",FACE,{"disambiguationData":[OSD([sQuery(id+"F16.wireOp",EDGE,"E76"),sQuery(id+"F16.wireOp",EDGE,"E80"),sQuery(id+"F16.wireOp",EDGE,"E81.filletArc"),sQuery(id+"F17.wireOp",EDGE,"E85"),sQuery(id+"F17.wireOp",EDGE,"E87"),sQuery(id+"F17.wireOp",EDGE,"E91.filletArc")])]}),makeQuery(id+"F31.opExtrude","SWEPT_FACE",FACE,{"disambiguationData":[OSD([sQuery(id+"F30.wireOp",EDGE,"E169.right")])]})]});
            var Q7;
            Q7=makeQuery(id+"F31.boolean.opBoolean","INTERSECT",EDGE,{"derivedFrom":[makeQuery(id+"F20.opLoft","SWEPT_FACE",FACE,{"disambiguationData":[OSD([sQuery(id+"F16.wireOp",EDGE,"E76"),sQuery(id+"F16.wireOp",EDGE,"E80"),sQuery(id+"F16.wireOp",EDGE,"E81.filletArc"),sQuery(id+"F17.wireOp",EDGE,"E85"),sQuery(id+"F17.wireOp",EDGE,"E87"),sQuery(id+"F17.wireOp",EDGE,"E91.filletArc")])]}),makeQuery(id+"F31.opExtrude","SWEPT_FACE",FACE,{"disambiguationData":[OSD([sQuery(id+"F30.wireOp",EDGE,"E169.bottom")])]})]});
            var Q8;
            Q8=makeQuery(id+"F31.boolean.opBoolean","INTERSECT",EDGE,{"derivedFrom":[makeQuery(id+"F20.opLoft","SWEPT_FACE",FACE,{"disambiguationData":[OSD([sQuery(id+"F16.wireOp",EDGE,"E76"),sQuery(id+"F16.wireOp",EDGE,"E80"),sQuery(id+"F16.wireOp",EDGE,"E81.filletArc"),sQuery(id+"F17.wireOp",EDGE,"E85"),sQuery(id+"F17.wireOp",EDGE,"E87"),sQuery(id+"F17.wireOp",EDGE,"E91.filletArc")])]}),makeQuery(id+"F31.opExtrude","SWEPT_FACE",FACE,{"disambiguationData":[OSD([sQuery(id+"F30.wireOp",EDGE,"E176")])]})]});
            var Q9;
            Q9=makeQuery(id+"F31.boolean.opBoolean","INTERSECT",EDGE,{"derivedFrom":[makeQuery(id+"F20.opLoft","SWEPT_FACE",FACE,{"disambiguationData":[OSD([sQuery(id+"F16.wireOp",EDGE,"E76"),sQuery(id+"F16.wireOp",EDGE,"E80"),sQuery(id+"F16.wireOp",EDGE,"E81.filletArc"),sQuery(id+"F17.wireOp",EDGE,"E85"),sQuery(id+"F17.wireOp",EDGE,"E87"),sQuery(id+"F17.wireOp",EDGE,"E91.filletArc")])]}),makeQuery(id+"F31.opExtrude","SWEPT_FACE",FACE,{"disambiguationData":[OSD([sQuery(id+"F30.wireOp",EDGE,"E173.left")])]})]});
            var Q10;
            Q10=makeQuery(id+"F31.boolean.opBoolean","INTERSECT",EDGE,{"derivedFrom":[makeQuery(id+"F20.opLoft","SWEPT_FACE",FACE,{"disambiguationData":[OSD([sQuery(id+"F16.wireOp",EDGE,"E76"),sQuery(id+"F16.wireOp",EDGE,"E80"),sQuery(id+"F16.wireOp",EDGE,"E81.filletArc"),sQuery(id+"F17.wireOp",EDGE,"E85"),sQuery(id+"F17.wireOp",EDGE,"E87"),sQuery(id+"F17.wireOp",EDGE,"E91.filletArc")])]}),makeQuery(id+"F31.opExtrude","SWEPT_FACE",FACE,{"disambiguationData":[OSD([sQuery(id+"F30.wireOp",EDGE,"E175")])]})]});
            var Q11;
            Q11=makeQuery(id+"F31.boolean.opBoolean","INTERSECT",EDGE,{"derivedFrom":[makeQuery(id+"F20.opLoft","SWEPT_FACE",FACE,{"disambiguationData":[OSD([sQuery(id+"F16.wireOp",EDGE,"E77"),sQuery(id+"F16.wireOp",EDGE,"E78"),sQuery(id+"F16.wireOp",EDGE,"E82.filletArc"),sQuery(id+"F17.wireOp",EDGE,"E86"),sQuery(id+"F17.wireOp",EDGE,"E90"),sQuery(id+"F17.wireOp",EDGE,"E92.filletArc")])]}),makeQuery(id+"F31.opExtrude","SWEPT_FACE",FACE,{"disambiguationData":[OSD([sQuery(id+"F30.wireOp",EDGE,"E175")])]})]});
            var Q12;
            Q12=makeQuery(id+"F31.boolean.opBoolean","INTERSECT",EDGE,{"derivedFrom":[makeQuery(id+"F20.opLoft","SWEPT_FACE",FACE,{"disambiguationData":[OSD([sQuery(id+"F16.wireOp",EDGE,"E77"),sQuery(id+"F16.wireOp",EDGE,"E78"),sQuery(id+"F16.wireOp",EDGE,"E82.filletArc"),sQuery(id+"F17.wireOp",EDGE,"E86"),sQuery(id+"F17.wireOp",EDGE,"E90"),sQuery(id+"F17.wireOp",EDGE,"E92.filletArc")])]}),makeQuery(id+"F31.opExtrude","SWEPT_FACE",FACE,{"disambiguationData":[OSD([sQuery(id+"F30.wireOp",EDGE,"E176")])]})]});
            var Q13;
            Q13=makeQuery(id+"F31.boolean.opBoolean","INTERSECT",EDGE,{"derivedFrom":[makeQuery(id+"F20.opLoft","SWEPT_FACE",FACE,{"disambiguationData":[OSD([sQuery(id+"F16.wireOp",EDGE,"E77"),sQuery(id+"F16.wireOp",EDGE,"E78"),sQuery(id+"F16.wireOp",EDGE,"E82.filletArc"),sQuery(id+"F17.wireOp",EDGE,"E86"),sQuery(id+"F17.wireOp",EDGE,"E90"),sQuery(id+"F17.wireOp",EDGE,"E92.filletArc")])]}),makeQuery(id+"F31.opExtrude","SWEPT_FACE",FACE,{"disambiguationData":[OSD([sQuery(id+"F30.wireOp",EDGE,"E174")])]})]});
            var Q14;
            Q14=makeQuery(id+"F31.boolean.opBoolean","INTERSECT",EDGE,{"derivedFrom":[makeQuery(id+"F20.opLoft","SWEPT_FACE",FACE,{"disambiguationData":[OSD([sQuery(id+"F16.wireOp",EDGE,"E77"),sQuery(id+"F16.wireOp",EDGE,"E78"),sQuery(id+"F16.wireOp",EDGE,"E82.filletArc"),sQuery(id+"F17.wireOp",EDGE,"E86"),sQuery(id+"F17.wireOp",EDGE,"E90"),sQuery(id+"F17.wireOp",EDGE,"E92.filletArc")])]}),makeQuery(id+"F31.opExtrude","SWEPT_FACE",FACE,{"disambiguationData":[OSD([sQuery(id+"F30.wireOp",EDGE,"E173.left")])]})]});
            fillet(context, id + "F32", {"entities" : qUnion([Q0, Q1, Q2, Q3, Q4, Q5, Q6, Q7, Q8, Q9, Q10, Q11, Q12, Q13, Q14]), "radius" : 2 * mm, "tangentPropagation" : true, "allowEdgeOverflow" : false});
        }
        {
            var Q0;
            Q0=makeQuery(id+"F31.boolean.opBoolean","INTERSECT",EDGE,{"derivedFrom":[makeQuery(id+"F20.opLoft","SWEPT_FACE",FACE,{"disambiguationData":[OSD([sQuery(id+"F16.wireOp",EDGE,"E76"),sQuery(id+"F16.wireOp",EDGE,"E80"),sQuery(id+"F16.wireOp",EDGE,"E81.filletArc"),sQuery(id+"F17.wireOp",EDGE,"E85"),sQuery(id+"F17.wireOp",EDGE,"E87"),sQuery(id+"F17.wireOp",EDGE,"E91.filletArc")])]}),makeQuery(id+"F31.opExtrude","SWEPT_FACE",FACE,{"disambiguationData":[OSD([sQuery(id+"F30.wireOp",EDGE,"E174")])]})]});
            fillet(context, id + "F33", {"entities" : qUnion([Q0]), "radius" : 15 * mm, "tangentPropagation" : true, "allowEdgeOverflow" : false});
        }
        {
            var Q0;
            Q0=makeQuery(id+"F20.opLoft","SWEPT_BODY",BODY,{"disambiguationData":[OSD([makeQuery(id+"F13.imprint","IMPRINT",FACE,{"disambiguationData":[TD([[makeQuery(id+"F13.imprint","IMPRINT",EDGE,{"derivedFrom":sQuery(id+"F13.wireOp",EDGE,"E45")}),-1.0]])]}),sQuery(id+"F14.wireOp",EDGE,"E55"),sQuery(id+"F15.wireOp",EDGE,"E65"),makeQuery(id+"F16.imprint","IMPRINT",FACE,{"disambiguationData":[TD([[makeQuery(id+"F16.imprint","IMPRINT",EDGE,{"derivedFrom":sQuery(id+"F16.wireOp",EDGE,"E75")}),-1.0]])]}),sQuery(id+"F17.wireOp",EDGE,"E85"),sQuery(id+"F18.wireOp",EDGE,"E95")])]});
            var Q1;
            Q1=qCreatedBy(makeId("Right.planeOp"),FACE);
            mirror(context, id + "F34", {"operationType" : NewBodyOperationType.ADD, "entities" : qUnion([Q0]), "mirrorPlane" : qUnion([Q1])});
        }
    });
